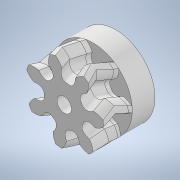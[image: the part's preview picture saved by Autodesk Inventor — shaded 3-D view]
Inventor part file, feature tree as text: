
AUTODESK INVENTOR PART (.ipt)
format: ipt  version: 2022 (Build 260153070, 153G)  size: 870,912 bytes
history: native  units: mm
features: sketch x5, extrude x3, helix x2, pattern_circular x1, mirror x1, revolve x1, projected_geometry x1
ambient origin geometry x8: Origin, YZ Plane, XZ Plane, XY Plane, X Axis, Y Axis, Z Axis, Center Point
bodies: Solid1 (feature_tree)
feature tree (14):
  sketch  "Sketch1"  dims[d0=1.5mm d1=0.0mm]
  extrude  "Extrusion1"  TaperAngle=0.0deg  [1 undecoded]
  helix  "Coil1"  [1 undecoded]
  pattern_circular  "Circular Pattern1"  [2 undecoded]
  mirror  "Mirror1"
  helix  "Coil2"  [1 undecoded]
  extrude  "Extrusion2"  Depth=2.15mm
  extrude  "Extrusion3"  Depth=2.15mm
  revolve  "Revolution1"  Angle=90.0deg
  sketch  "Sketch2"  dims[d2=64.295707mm d3=1.5mm d4=10.0mm d5=0.0mm d6=90.0deg d7=90.0deg d8=0.0mm d9=0.0mm d10=70.0mm d11=360.0deg]
  projected_geometry  "Projected Loop1"
  sketch  "Sketch3"  dims[d13=64.295707mm d14=0.5mm d15=10.0mm d16=0.0mm d17=90.0deg d18=90.0deg d19=0.0mm d20=0.0mm]
  sketch  "Sketch4"  dims[d21=2.75mm d22=0.0mm]
  sketch  "Sketch5"  dims[d23=6.2mm d24=2.0mm d25=0.0mm d26=0.875mm d27=1.5mm d28=2.15mm d29=90.0deg]
note: 5 required parameter values undecoded (feature->parameter linkage not recoverable at this tier; creation-order binding heuristic only, values carry confidence <= 0.55)
